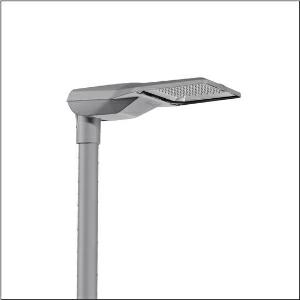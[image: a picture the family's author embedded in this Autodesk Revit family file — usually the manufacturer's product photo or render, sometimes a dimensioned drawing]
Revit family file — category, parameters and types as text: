
# Revit family: streetlight_sl_21_midi___st0_8a_5xe7c63a08nb_ed6b
name_source: partatom
category: Lighting Fixtures
units: mm (PartAtom-declared; Revit-internal decimal feet)

## family parameters
Cut with Voids When Loaded = No
Host = Face
Light Source = No
Part Type = Normal
Room Calculation Point = No
Round Connector Dimension = Use Diameter
Shared = No

## types (1)
- --- (1 x LED, 20350 lm, 151.2 W, 2700K)
    Apparent Load = 151 VA
    CIE Flux Codes = 41 75 97 100 100
    Color Rendering = 70
    Color Temperature = 2700K
    Default Elevation = 1800 mm
    Description = Streetlight SL 21 midi, mast luminaire, primary light control with lens, of PMMA, primary optical cover: cover, of toughened safety glass, transparent, light distribution: ST0.8a, light emission: direct distribution, primary light characteristic: asymmetric, installation type: post-top, side-entry, LED, 3G 1.5mm², High Power LED, rated luminous flux: 20.350lm, luminous efficacy: 135lm/W, light colour: 727, colour temperature: 2700K, control: overheat protection, constant luminous flux control, time-dependent luminous flux control, flexible luminous flux parameterisation, mains connection: 220..240V, AC, 50/60Hz, connection cable pre-assembled, cable length: 12,5m, wiring characteristics: H07RN-F, start of lifetime: 151W, end of service life: 157W, reduction: 70W, luminaire housing, of diecast aluminium, powder-coated, Siteco® metallic grey (DB 702S), corrosivity category C5 mid according to DIN EN ISO 12944, please order mast flange separately, inclination adjustable: 0°, 5°, 10°, 15°, sealing non-destructively replaceable, multi-level sealing system, length: 644mm, width: 335mm, height: 110mm, mast flange for spigot size: 42mm (side-entry): 5XC10008XM4, 60/48mm (side-entry/post-top): 5XC10108XM2, 76/60mm (side-entry/post-top): 5XC10108XM1, protection rating (complete): IP66, insulation class (complete): insulation class II (safety insulation), certification: CE, ENEC, ENEC+, VDE, impact resistance: IK09, permissible operating ambient temperature for outdoor applications: -40..+50°C, standard-compliant lighting for roads and squares, packaging unit: 1 piece

Light Distribution: ST0.8a
    Height = 111 mm
    Lamp = 1 x LED
    Lamp Light Flux = 20350 lm
    Lamp Power = 151.2 W
    Lamp count = 1
    Length = 644 mm
    Luminous efficacy = 135 lm/W
    Manufacturer = Siteco
    ModVariant = No
    Model = 5XE7C63A08NB
    Number of Poles = 1
    OnlyDefault = Yes
    Power Factor = 1
    Product Name = Streetlight SL 21 midi | ST0.8a
    Product group = mast luminaire | pylon top
    ProductGroupID = 6100
    Protection Class = Protection class II
    Protection Degree = IP 66
    RLX_Detail_Level = 1
    RLX_Emergency_Light_Flux = 0 lm
    RLX_Emergency_Type = 0
    RLX_Emergency_Type_DB = No
    RlxData = <blob elided: 90773 chars, md5=4f77f32e>
    Socket = socket
    Standby Power = 0 W
    System Light Flux = 20350 lm
    System Power = 151 W
    Type Comments = factory setting: luminous flux: 100 % | Output Level: 100 % | 802 mA
    Type Image = l_1004298.jpg
    URL = http://relux.com
    VarID = @adj_100845
    Voltage = 0 V
    Weight = 0.00 kg
    Width = 336 mm

## geometry (parser evidence)
native form markers: Blend x4, Sweep x11
no freeform markers — native parametric forms only
